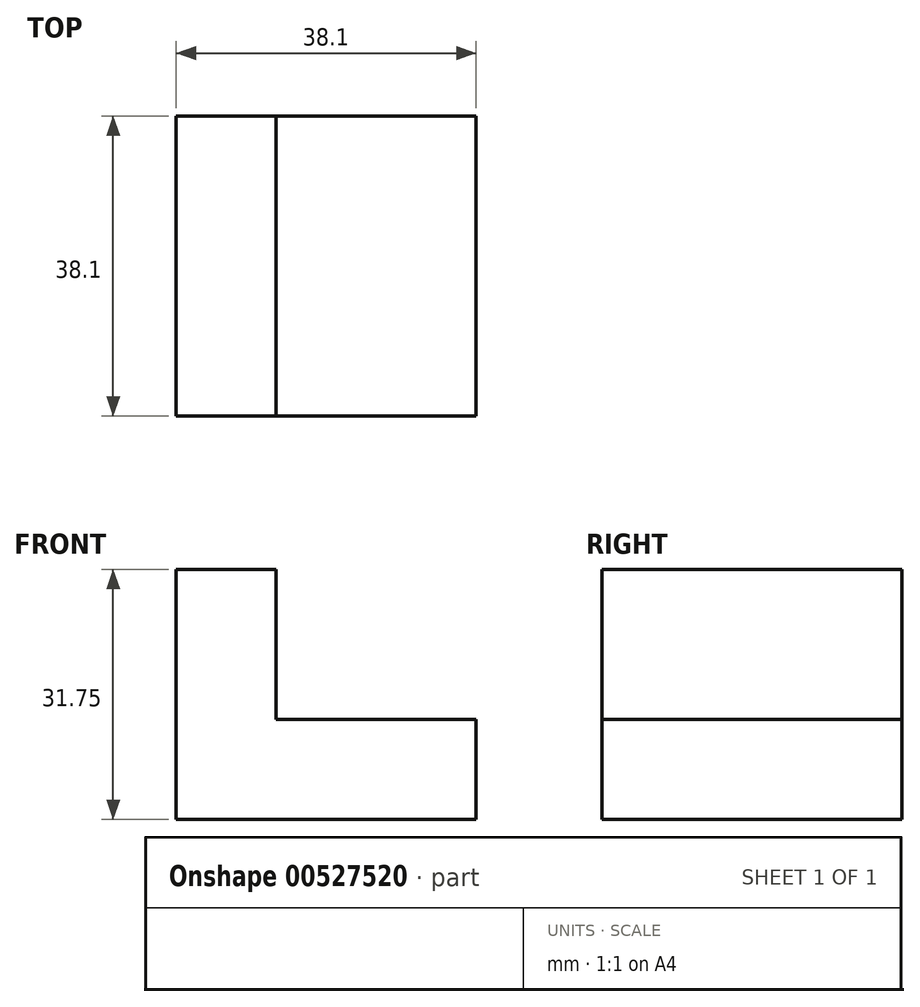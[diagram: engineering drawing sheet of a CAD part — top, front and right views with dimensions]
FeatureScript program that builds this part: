
annotation { "Feature Type Name" : "Feature", "Feature Type Description" : "" }
export const myFeature = defineFeature(function(context is Context, id is Id, definition is map)
    precondition{}
    {
        {
            var Q0;
            Q0=qCreatedBy(makeId("Front.planeOp"),FACE);
            var sketch = newSketch(context, id + "F0", { "sketchPlane" : qUnion([Q0])});
            skLineSegment(sketch, "E0", {"start": v(0, 0) * mm, "end": v(38.1, 0) * mm});
            skLineSegment(sketch, "E1", {"start": v(38.1, 0) * mm, "end": v(38.1, 12.7) * mm});
            skLineSegment(sketch, "E2", {"start": v(38.1, 12.7) * mm, "end": v(12.7, 12.7) * mm});
            skLineSegment(sketch, "E3", {"start": v(12.7, 12.7) * mm, "end": v(12.7, 31.75) * mm});
            skLineSegment(sketch, "E4", {"start": v(12.7, 31.75) * mm, "end": v(0, 31.75) * mm});
            skLineSegment(sketch, "E5", {"start": v(0, 31.75) * mm, "end": v(0, 0) * mm});
            skSolve(sketch);
        }
        {
            var Q0;
            Q0=makeQuery(id+"F0.imprint","IMPRINT",FACE,{"disambiguationData":[TD([[makeQuery(id+"F0.imprint","IMPRINT",EDGE,{"derivedFrom":sQuery(id+"F0.wireOp",EDGE,"E0")}),1.0]])]});
            extrude(context, id + "F1", {"entities" : qUnion([Q0]), "depth" : 38.1 * mm, "offsetDistance" : 25.4 * mm});
        }
    });
